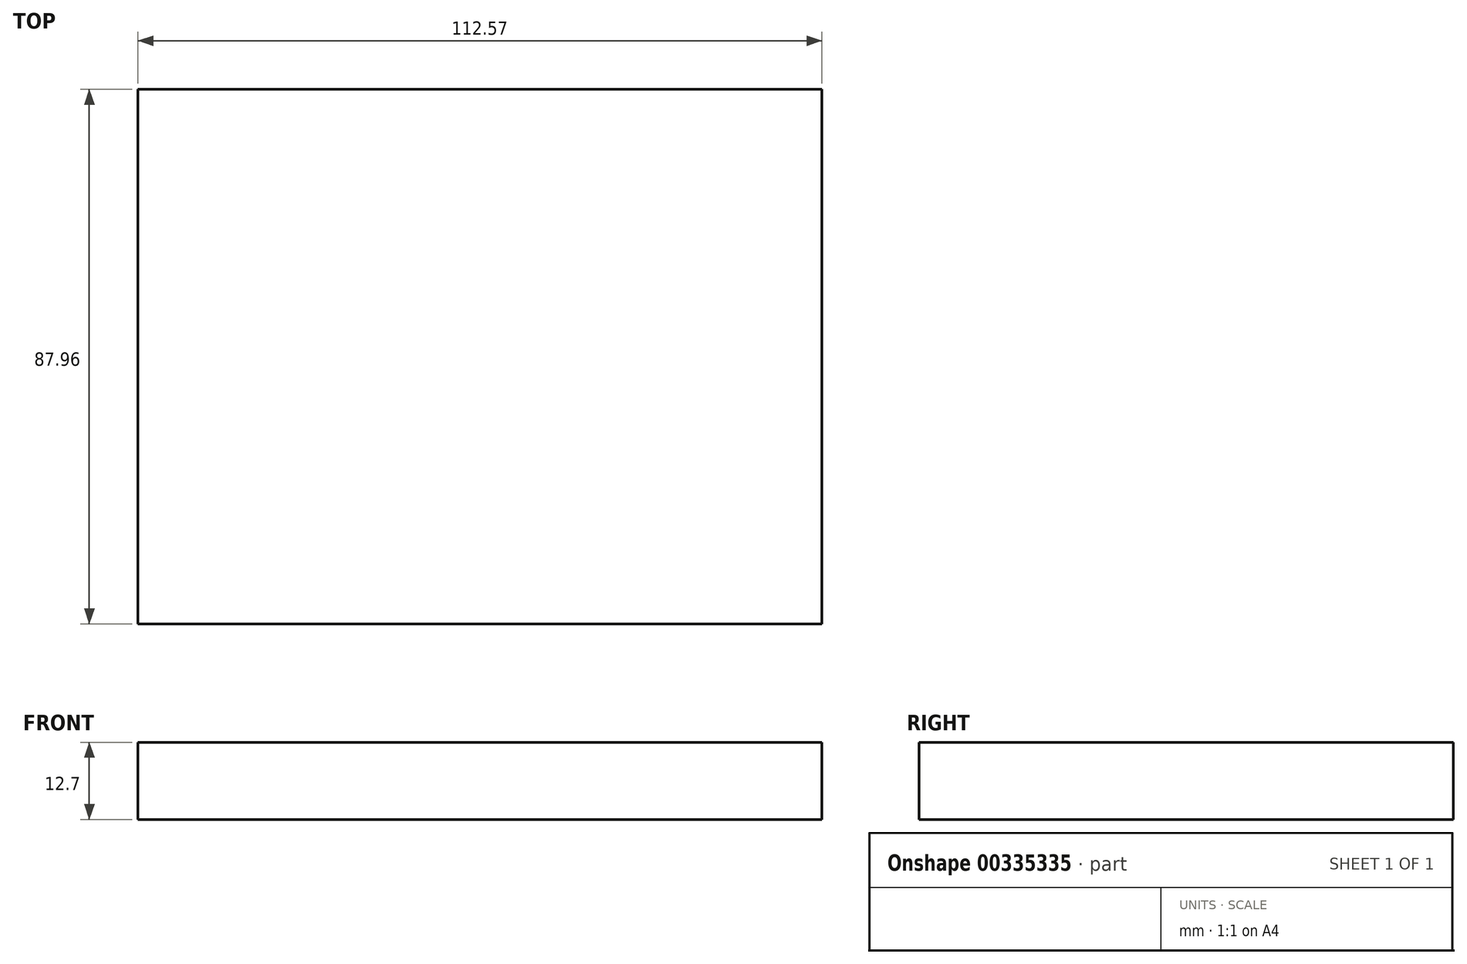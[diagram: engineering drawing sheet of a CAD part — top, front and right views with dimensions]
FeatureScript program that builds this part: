
annotation { "Feature Type Name" : "Feature", "Feature Type Description" : "" }
export const myFeature = defineFeature(function(context is Context, id is Id, definition is map)
    precondition{}
    {
        {
            var Q0;
            Q0=qCreatedBy(makeId("Top.planeOp"),FACE);
            var sketch = newSketch(context, id + "F0", { "sketchPlane" : qUnion([Q0])});
            skLineSegment(sketch, "E0.bottom", {"start": v(-55.89, 52.21) * mm, "end": v(56.68, 52.21) * mm});
            skLineSegment(sketch, "E0.top", {"start": v(-55.89, -35.75) * mm, "end": v(56.68, -35.75) * mm});
            skLineSegment(sketch, "E0.left", {"start": v(-55.89, 52.21) * mm, "end": v(-55.89, -35.75) * mm});
            skLineSegment(sketch, "E0.right", {"start": v(56.68, 52.21) * mm, "end": v(56.68, -35.75) * mm});
            skSolve(sketch);
        }
        {
            var Q0;
            Q0 = qSketchRegion(id + "F0", true);
            extrude(context, id + "F1", {"entities" : qUnion([Q0]), "oppositeDirection" : true, "depth" : 12.7 * mm});
        }
        {
            var Q0;
            Q0=makeQuery(id+"F1.opExtrude","CAP_FACE",FACE,{"disambiguationData":[OSD([sQuery(id+"F0.wireOp",EDGE,"E0.bottom"),sQuery(id+"F0.wireOp",EDGE,"E0.top"),sQuery(id+"F0.wireOp",EDGE,"E0.left"),sQuery(id+"F0.wireOp",EDGE,"E0.right")])],"isStart":true});
            var sketch = newSketch(context, id + "F2", { "sketchPlane" : qUnion([Q0])});
            skSolve(sketch);
        }
        {
            var Q0;
            Q0=makeQuery(id+"F1.opExtrude","CAP_FACE",FACE,{"disambiguationData":[OSD([sQuery(id+"F0.wireOp",EDGE,"E0.bottom"),sQuery(id+"F0.wireOp",EDGE,"E0.top"),sQuery(id+"F0.wireOp",EDGE,"E0.left"),sQuery(id+"F0.wireOp",EDGE,"E0.right")])],"isStart":false});
            var sketch = newSketch(context, id + "F3", { "sketchPlane" : qUnion([Q0])});
            skCircle(sketch, "E1", {"center": v(-35.5, 16.83) * mm, "radius": 6.35 * mm});
            skCircle(sketch, "E2", {"center": v(-35.5, -31.07) * mm, "radius": 6.35 * mm});
            skCircle(sketch, "E3", {"center": v(35.54, 16.83) * mm, "radius": 6.35 * mm});
            skCircle(sketch, "E4", {"center": v(37, -31.07) * mm, "radius": 6.35 * mm});
            skSolve(sketch);
        }
        {
            var Q0;
            Q0=sQuery(id+"F3.wireOp",EDGE,"E1");
            var Q1;
            Q1=sQuery(id+"F3.wireOp",EDGE,"E2");
            var Q2;
            Q2=sQuery(id+"F3.wireOp",EDGE,"E3");
            var Q3;
            Q3=sQuery(id+"F3.wireOp",EDGE,"E4");
            extrude(context, id + "F4", {"bodyType" : ToolBodyType.SURFACE, "surfaceEntities" : qUnion([Q0, Q1, Q2, Q3]), "depth" : 127 * mm});
        }
    });
